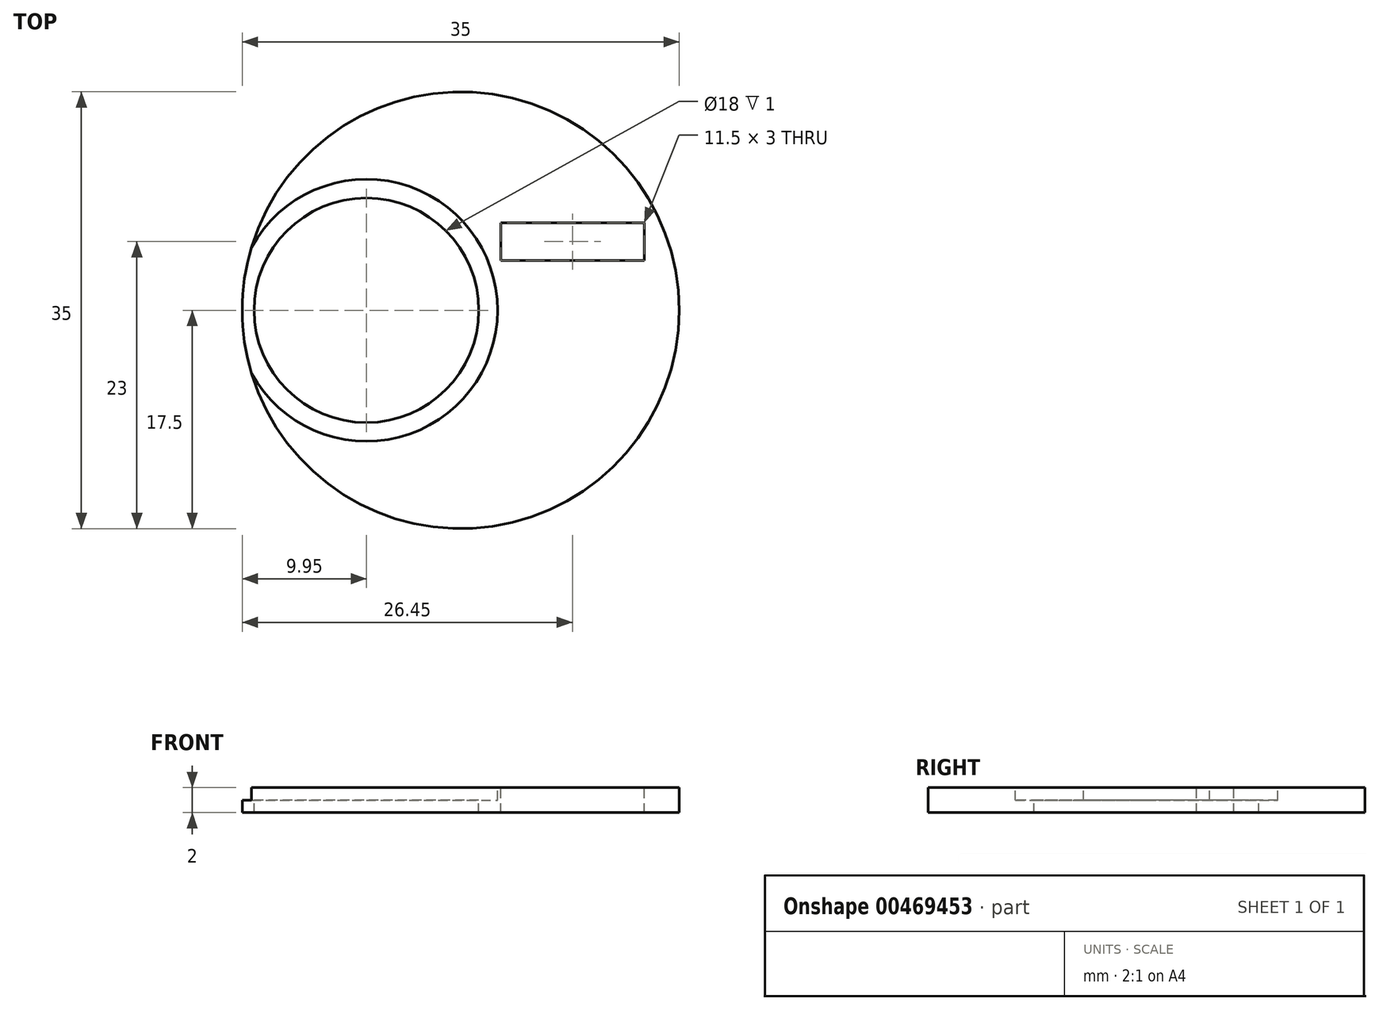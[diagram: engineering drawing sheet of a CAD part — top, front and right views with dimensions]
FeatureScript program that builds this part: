
annotation { "Feature Type Name" : "Feature", "Feature Type Description" : "" }
export const myFeature = defineFeature(function(context is Context, id is Id, definition is map)
    precondition{}
    {
        {
            var Q0;
            Q0=qCreatedBy(makeId("Top.planeOp"),FACE);
            var sketch = newSketch(context, id + "F0", { "sketchPlane" : qUnion([Q0])});
            skCircle(sketch, "E0", {"center": v(0, 0) * mm, "radius": 17.5 * mm});
            skPoint(sketch, "E1.center.orphan", {"position": v(-52.49, -0.84) * mm});
            skCircle(sketch, "E2", {"center": v(-7.55, 0) * mm, "radius": 9 * mm});
            skLineSegment(sketch, "E3.bottom", {"start": v(3.2, -6.5) * mm, "end": v(14.7, -6.5) * mm});
            skLineSegment(sketch, "E3.top", {"start": v(3.2, 7) * mm, "end": v(14.7, 7) * mm});
            skLineSegment(sketch, "E3.left", {"start": v(3.2, -6.5) * mm, "end": v(3.2, 7) * mm});
            skLineSegment(sketch, "E3.right", {"start": v(14.7, -6.5) * mm, "end": v(14.7, 7) * mm});
            skLineSegment(sketch, "E4.bottom", {"start": v(3.2, 4) * mm, "end": v(14.7, 4) * mm});
            skLineSegment(sketch, "E4.left", {"start": v(3.2, 4) * mm, "end": v(3.2, 7) * mm});
            skLineSegment(sketch, "E4.right", {"start": v(14.7, 4) * mm, "end": v(14.7, 7) * mm});
            skCircle(sketch, "E5", {"center": v(-7.55, 0) * mm, "radius": 10.5 * mm});
            skSolve(sketch);
        }
        {
            var Q0;
            Q0=makeQuery(id+"F0.imprint","IMPRINT",FACE,{"disambiguationData":[TD([[makeQuery(id+"F0.imprint","IMPRINT",EDGE,{"derivedFrom":sQuery(id+"F0.wireOp",EDGE,"E0")}),1.0]])]});
            var Q1;
            Q1=makeQuery(id+"F0.imprint","IMPRINT",FACE,{"disambiguationData":[TD([[makeQuery(id+"F0.imprint","IMPRINT",EDGE,{"derivedFrom":sQuery(id+"F0.wireOp",EDGE,"E2")}),-1.0]])]});
            var Q2;
            Q2=makeQuery(id+"F0.imprint","IMPRINT",FACE,{"disambiguationData":[TD([[makeQuery(id+"F0.imprint","IMPRINT",EDGE,{"derivedFrom":sQuery(id+"F0.wireOp",EDGE,"E3.bottom")}),1.0]])]});
            var Q3;
            Q3=makeQuery(id+"F0.imprint","IMPRINT",FACE,{"disambiguationData":[TD([[makeQuery(id+"F0.imprint","IMPRINT",EDGE,{"derivedFrom":sQuery(id+"F0.wireOp",EDGE,"E3.bottom")}),-1.0]])]});
            extrude(context, id + "F1", {"entities" : qUnion([Q0, Q1, Q2, Q3]), "oppositeDirection" : true, "depth" : 2 * mm});
        }
        {
            var Q0;
            Q0=makeQuery(id+"F0.imprint","IMPRINT",FACE,{"disambiguationData":[TD([[makeQuery(id+"F0.imprint","IMPRINT",EDGE,{"derivedFrom":sQuery(id+"F0.wireOp",EDGE,"E2")}),-1.0]])]});
            extrude(context, id + "F2", {"entities" : qUnion([Q0]), "operationType" : NewBodyOperationType.REMOVE, "oppositeDirection" : true, "depth" : 1 * mm});
        }
    });
